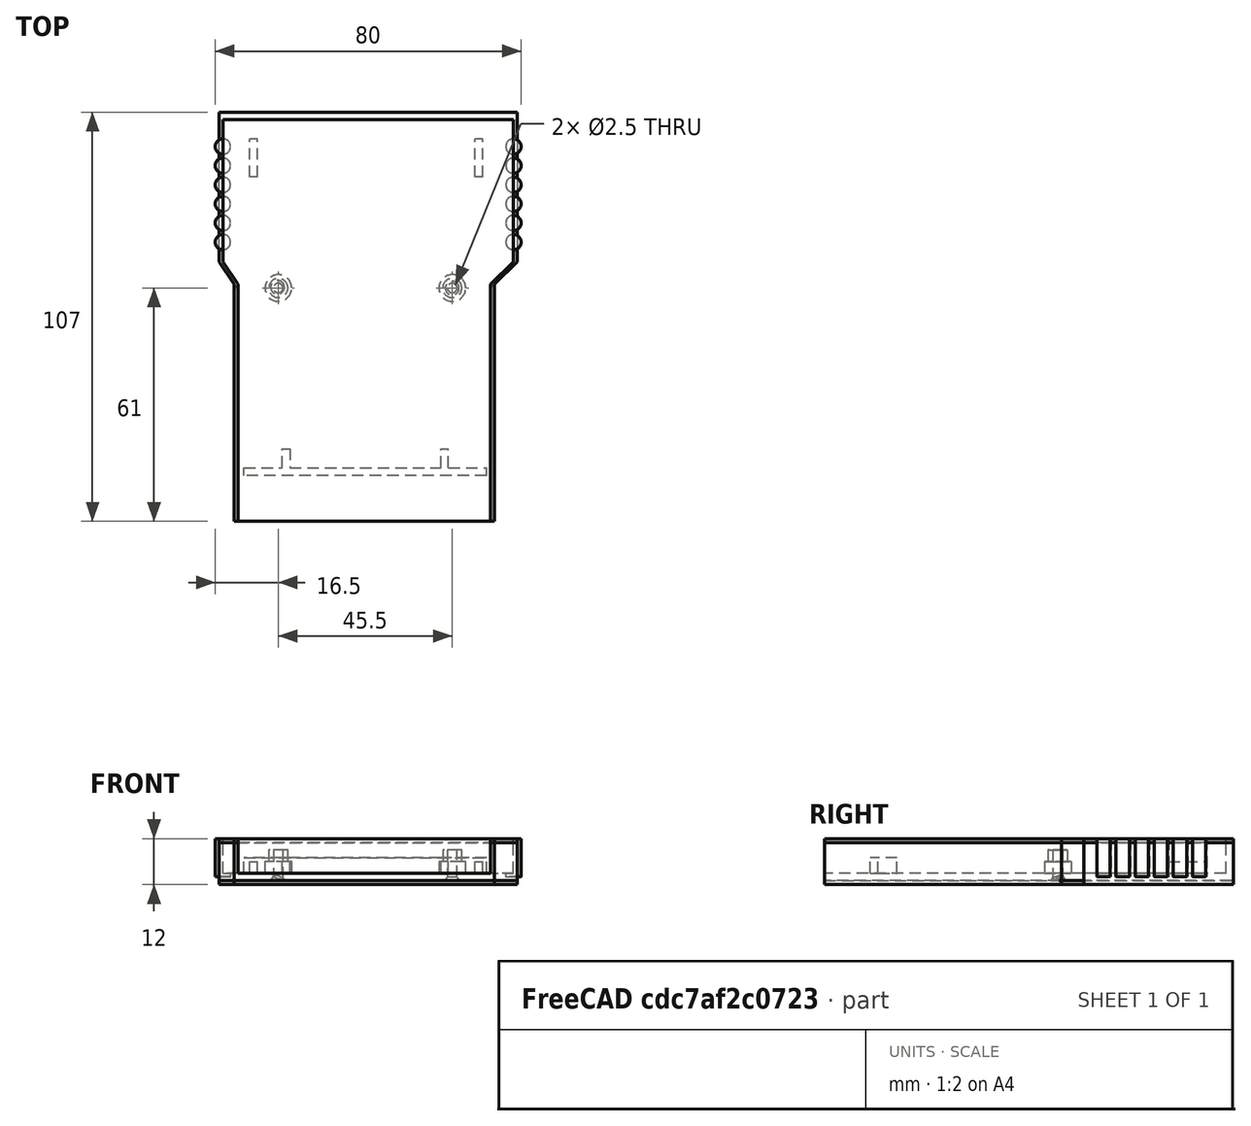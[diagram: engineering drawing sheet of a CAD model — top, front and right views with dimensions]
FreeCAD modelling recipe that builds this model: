
FCSTD DOCUMENT  (FreeCAD 0.20R29410 (Git))
Label: RTO11a_Cart_Bottom
License: All rights reserved
LicenseURL: http://en.wikipedia.org/wiki/All_rights_reserved
objects: Part::Cylinder×18, Part::MultiFuse×11, Part::Cut×8, Part::Fillet×5, Part::Box×4, PartDesign::Pad×4, Sketcher::SketchObject×3, Part::Cone×2, PartDesign::Body×2, Mesh::Feature×1, Part::Feature×1
note: 62 computed .brp shape members not serialized (recipe doc carries the construction recipe); baked Part::Feature solids carry a one-line shape summary decoded from their .brp

FEATURE [Part::Cylinder] Cylinder001  label="Cilindro"
  Angle = 360
  AttacherType = Attacher::AttachEngine3D
  FirstAngle = 0
  Height = 16
  Placement = pos=(-11,61,-2) rot=(0,0,1;0rad)
  Radius = 1.25
  SecondAngle = 0
FEATURE [Part::Cylinder] Cylinder002  label="Cilindro001"
  Angle = 360
  AttacherType = Attacher::AttachEngine3D
  FirstAngle = 0
  Height = 20
  Placement = pos=(-56.5,61,-2) rot=(0,0,1;0rad)
  Radius = 1.25
  SecondAngle = 0
FEATURE [Part::Cone] Cone  label="Cono"
  Angle = 360
  AttacherType = Attacher::AttachEngine3D
  Height = 5
  Placement = pos=(-11,61,-2) rot=(0,0,1;3.14159rad)
  Radius1 = 3
  Radius2 = 0
FEATURE [Part::Cone] Cone001  label="Cono001"
  Angle = 360
  AttacherType = Attacher::AttachEngine3D
  Height = 5
  Placement = pos=(-56.7,61.2,-2) rot=(0,0,1;0.017453rad)
  Radius1 = 3
  Radius2 = 0
FEATURE [Part::Box] Box001  label="Cubo001"
  AttacherType = Attacher::AttachEngine3D
  Height = 4
  Length = 2
  Placement = pos=(-64,90,1) rot=(0,0,1;0rad)
  Width = 10
FEATURE [Part::Cylinder] Cylinder003  label="Cilindro002"
  Angle = 360
  AttacherType = Attacher::AttachEngine3D
  FirstAngle = 0
  Height = 4
  Placement = pos=(-11,61,1) rot=(0,0,1;0rad)
  Radius = 3.5
  SecondAngle = 0
FEATURE [Part::MultiFuse] Fusion003
  Shapes = -> [Cylinder003,Box001]
FEATURE [Part::Cylinder] Cylinder004  label="Cilindro003"
  Angle = 360
  AttacherType = Attacher::AttachEngine3D
  FirstAngle = 0
  Height = 4
  Placement = pos=(-11,61,4) rot=(0,0,1;0rad)
  Radius = 2.5
  SecondAngle = 0
FEATURE [Part::MultiFuse] Fusion004
  Shapes = -> [Fusion003,Cylinder004]
FEATURE [Part::Cylinder] Cylinder  label="Cilindro004"
  Angle = 360
  AttacherType = Attacher::AttachEngine3D
  FirstAngle = 0
  Height = 4
  Placement = pos=(-56.5,61,1) rot=(0,0,1;0rad)
  Radius = 3.5
  SecondAngle = 0
FEATURE [Part::Cylinder] Cylinder005  label="Cilindro005"
  Angle = 360
  AttacherType = Attacher::AttachEngine3D
  FirstAngle = 0
  Height = 3
  Placement = pos=(-56.5,61,5) rot=(0,0,1;0rad)
  Radius = 2.5
  SecondAngle = 0
FEATURE [Sketcher::SketchObject] Sketch004
  AttachmentOffset = pos=(0,0,1) rot=(0,0,1;0rad)
  FullyConstrained = true
  MapMode = 5
  Placement = pos=(0,0,1) rot=(0,0,1;0rad)
  Support = -> [XY_Plane]
  sketch-geometry (12):
    g0: LineSegment StartX=-65.5 StartY=12 StartZ=0 EndX=-2 EndY=12 EndZ=0
    g1: LineSegment StartX=-2 StartY=14 StartZ=0 EndX=-12 EndY=14 EndZ=0
    g2: LineSegment StartX=-12 StartY=19 StartZ=0 EndX=-14 EndY=19 EndZ=0
    g3: LineSegment StartX=-12 StartY=19 StartZ=0 EndX=-12 EndY=14 EndZ=0
    g4: LineSegment StartX=-14 StartY=19 StartZ=0 EndX=-14 EndY=14 EndZ=0
    g5: LineSegment StartX=-14 StartY=14 StartZ=0 EndX=-53.5 EndY=14 EndZ=0
    g6: LineSegment StartX=-53.5 StartY=14 StartZ=0 EndX=-53.5 EndY=19 EndZ=0
    g7: LineSegment StartX=-53.5 StartY=19 StartZ=0 EndX=-55.5 EndY=19 EndZ=0
    g8: LineSegment StartX=-55.5 StartY=19 StartZ=0 EndX=-55.5 EndY=14 EndZ=0
    g9: LineSegment StartX=-55.5 StartY=14 StartZ=0 EndX=-65.5 EndY=14 EndZ=0
    g10: LineSegment StartX=-65.5 StartY=14 StartZ=0 EndX=-65.5 EndY=12 EndZ=0
    g11: LineSegment StartX=-2 StartY=14 StartZ=0 EndX=-2 EndY=12 EndZ=0
  constraints (36):
    c: Horizontal(g0)
    c: Horizontal(g1)
    c: Coincident(g3,g2)
    c: Coincident(g3,g1)
    c: Coincident(g4,g2)
    c: Vertical(g4)
    c: Coincident(g5,g4)
    c: Horizontal(g5)
    c: Coincident(g6,g5)
    c: Vertical(g6)
    c: Coincident(g7,g6)
    c: Coincident(g7,g8)
    c: Vertical(g8)
    c: Coincident(g8,g9)
    c: Horizontal(g9)
    c: Coincident(g9,g10)
    c: Coincident(g10,g0)
    c: Horizontal(g7)
    c: Vertical(g10)
    c: Vertical(g3)
    c: DistanceY(g0,g9) = 2
    c: DistanceX(g7,g7) = 2
    c: DistanceX(g2,g2) = 2
    c: DistanceY(g4,g4) = 5
    c: DistanceY(g0,g1) = 2
    c: DistanceY(g8,g5) = 0
    c: Horizontal(g2)
    c: DistanceX(g0,g0) = 63.5
    c: DistanceX(g9,g9) = 10
    c: DistanceX(g1,g1) = 10
    c: DistanceY(g8,g8) = 5
    c: Coincident(g11,g1)
    c: Coincident(g11,g0)
    c: Vertical(g11)
    c: DistanceY(g-1,g0) = 12
    c: DistanceX(g0,g-1) = 2
FEATURE [PartDesign::Pad] Pad013  label="front_bar"
  Direction = (0,0,1)
  Length = 5
  Length2 = 10
  Profile = -> Sketch004
  ReferenceAxis = -> Sketch004 [N_Axis]
  Type = 0
FEATURE [Sketcher::SketchObject] Sketch
  FullyConstrained = true
  MapMode = 5
  Support = -> [XY_Plane]
  sketch-geometry (8):
    g0: LineSegment StartX=0 StartY=0 StartZ=0 EndX=-68 EndY=0 EndZ=0
    g1: LineSegment StartX=-68 StartY=0 StartZ=0 EndX=-68 EndY=62 EndZ=0
    g2: LineSegment StartX=-68 StartY=62 StartZ=0 EndX=-72 EndY=67.82 EndZ=0
    g3: LineSegment StartX=-72 StartY=67.82 StartZ=0 EndX=-72 EndY=107 EndZ=0
    g4: LineSegment StartX=-72 StartY=107 StartZ=0 EndX=6 EndY=107 EndZ=0
    g5: LineSegment StartX=6 StartY=107 StartZ=0 EndX=6 EndY=67.82 EndZ=0
    g6: LineSegment StartX=6 StartY=67.82 StartZ=0 EndX=0 EndY=62 EndZ=0
    g7: LineSegment StartX=0 StartY=62 StartZ=0 EndX=0 EndY=0 EndZ=0
  constraints (24):
    c: PointOnObject(g0,g-2)
    c: PointOnObject(g0,g-1)
    c: Horizontal(g0)
    c: Coincident(g0,g1)
    c: Vertical(g1)
    c: Coincident(g1,g2)
    c: Coincident(g2,g3)
    c: Vertical(g3)
    c: Coincident(g3,g4)
    c: Horizontal(g4)
    c: Coincident(g4,g5)
    c: Vertical(g5)
    c: Coincident(g5,g6)
    c: PointOnObject(g6,g-2)
    c: Coincident(g6,g7)
    c: DistanceY(g1,g1) = 62
    c: DistanceY(g7,g7) = 62
    c: Coincident(g0,g7)
    c: DistanceX(g4,g4) = 78
    c: DistanceX(g0,g0) = 68
    c: Distance(g1,g4) = 45
    c: DistanceX(g2,g1) = 4
    c: DistanceY(g5,g2) = 0
    c: DistanceY(g6,g5) = 5.82
FEATURE [PartDesign::Pad] Pad
  BaseFeature = -> Pad013
  Direction = (0,0,1)
  Length = 11
  Length2 = 10
  Profile = -> Sketch
  ReferenceAxis = -> Sketch [N_Axis]
  Type = 0
FEATURE [Sketcher::SketchObject] Sketch005
  AttachmentOffset = pos=(-1,0,2) rot=(0,0,1;0rad)
  FullyConstrained = true
  MapMode = 5
  Placement = pos=(-1,0,2) rot=(0,0,1;0rad)
  Support = -> [XY_Plane002]
  sketch-geometry (8):
    g0: LineSegment StartX=0 StartY=0 StartZ=0 EndX=-66 EndY=0 EndZ=0
    g1: LineSegment StartX=-66 StartY=0 StartZ=0 EndX=-66 EndY=62 EndZ=0
    g2: LineSegment StartX=-66 StartY=62 StartZ=0 EndX=-70 EndY=67.82 EndZ=0
    g3: LineSegment StartX=-70 StartY=67.82 StartZ=0 EndX=-70 EndY=105 EndZ=0
    g4: LineSegment StartX=-70 StartY=105 StartZ=0 EndX=6 EndY=105 EndZ=0
    g5: LineSegment StartX=6 StartY=105 StartZ=0 EndX=6 EndY=67.82 EndZ=0
    g6: LineSegment StartX=6 StartY=67.82 StartZ=0 EndX=0 EndY=62 EndZ=0
    g7: LineSegment StartX=0 StartY=62 StartZ=0 EndX=0 EndY=0 EndZ=0
  constraints (24):
    c: PointOnObject(g0,g-2)
    c: PointOnObject(g0,g-1)
    c: Horizontal(g0)
    c: Coincident(g0,g1)
    c: Vertical(g1)
    c: Coincident(g1,g2)
    c: Coincident(g2,g3)
    c: Vertical(g3)
    c: Coincident(g3,g4)
    c: Horizontal(g4)
    c: Coincident(g4,g5)
    c: Vertical(g5)
    c: Coincident(g5,g6)
    c: PointOnObject(g6,g-2)
    c: Coincident(g6,g7)
    c: DistanceY(g1,g1) = 62
    c: DistanceY(g7,g7) = 62
    c: Coincident(g0,g7)
    c: DistanceX(g4,g4) = 76
    c: DistanceX(g0,g0) = 66
    c: Distance(g1,g4) = 43
    c: DistanceX(g2,g1) = 4
    c: DistanceY(g5,g2) = 0
    c: DistanceY(g6,g5) = 5.82
FEATURE [PartDesign::Pad] Pad014
  BaseFeature = -> Pad
  Direction = (0,0,1)
  Length = 10
  Length2 = 10
  Profile = -> Sketch005
  ReferenceAxis = -> Sketch005 [N_Axis]
  Type = 0
FEATURE [PartDesign::Body] Body001  label="slot"
  Origin = -> Origin
  Placement = pos=(0,0,-1) rot=(0,0,1;0rad)
  Tip = -> Pad014
FEATURE [PartDesign::Pad] Pad015
  Direction = (0,0,1)
  Length = 10
  Length2 = 10
  Profile = -> Sketch005
  ReferenceAxis = -> Sketch005 [N_Axis]
  Type = 0
FEATURE [PartDesign::Body] Body  label="Base"
  Group = -> [Sketch005,Pad015]
  Origin = -> Origin001
  Tip = -> Pad015
FEATURE [Part::Cut] Cut013  label="Basevuota"
  Base = -> Pad014
  Tool = -> Body
FEATURE [Part::Box] Box  label="Cubo"
  AttacherType = Attacher::AttachEngine3D
  Height = 4
  Length = 2
  Placement = pos=(-5,90,1) rot=(0,0,1;0rad)
  Width = 10
FEATURE [Part::Cylinder] Cylinder006  label="Cilindro006"
  Angle = 360
  AttacherType = Attacher::AttachEngine3D
  FirstAngle = 0
  Height = 10
  Placement = pos=(5,78,1) rot=(0,0,1;0rad)
  Radius = 2
  SecondAngle = 0
FEATURE [Part::Cylinder] Cylinder007  label="Cilindro007"
  Angle = 360
  AttacherType = Attacher::AttachEngine3D
  FirstAngle = 0
  Height = 10
  Placement = pos=(5,73,1) rot=(0,0,1;0rad)
  Radius = 2
  SecondAngle = 0
FEATURE [Part::Cylinder] Cylinder008  label="Cilindro008"
  Angle = 360
  AttacherType = Attacher::AttachEngine3D
  FirstAngle = 0
  Height = 10
  Placement = pos=(5,83,1) rot=(0,0,1;0rad)
  Radius = 2
  SecondAngle = 0
FEATURE [Part::Cylinder] Cylinder009  label="Cilindro009"
  Angle = 360
  AttacherType = Attacher::AttachEngine3D
  FirstAngle = 0
  Height = 10
  Placement = pos=(5,88,1) rot=(0,0,1;0rad)
  Radius = 2
  SecondAngle = 0
FEATURE [Part::Cylinder] Cylinder010  label="Cilindro010"
  Angle = 360
  AttacherType = Attacher::AttachEngine3D
  FirstAngle = 0
  Height = 10
  Placement = pos=(5,93,1) rot=(0,0,1;0rad)
  Radius = 2
  SecondAngle = 0
FEATURE [Part::Cylinder] Cylinder011  label="Cilindro011"
  Angle = 360
  AttacherType = Attacher::AttachEngine3D
  FirstAngle = 0
  Height = 10
  Placement = pos=(5,98,1) rot=(0,0,1;0rad)
  Radius = 2
  SecondAngle = 0
FEATURE [Part::MultiFuse] Fusion009  label="cil_rx"
  Shapes = -> [Cylinder006,Cylinder007,Cylinder008,Cylinder009,Cylinder010,Cylinder011]
FEATURE [Part::Cylinder] Cylinder012  label="Cilindro012"
  Angle = 360
  AttacherType = Attacher::AttachEngine3D
  FirstAngle = 0
  Height = 10
  Placement = pos=(5,78,1) rot=(0,0,1;0rad)
  Radius = 2
  SecondAngle = 0
FEATURE [Part::Cylinder] Cylinder013  label="Cilindro013"
  Angle = 360
  AttacherType = Attacher::AttachEngine3D
  FirstAngle = 0
  Height = 10
  Placement = pos=(5,73,1) rot=(0,0,1;0rad)
  Radius = 2
  SecondAngle = 0
FEATURE [Part::Cylinder] Cylinder014  label="Cilindro014"
  Angle = 360
  AttacherType = Attacher::AttachEngine3D
  FirstAngle = 0
  Height = 10
  Placement = pos=(5,83,1) rot=(0,0,1;0rad)
  Radius = 2
  SecondAngle = 0
FEATURE [Part::Cylinder] Cylinder015  label="Cilindro015"
  Angle = 360
  AttacherType = Attacher::AttachEngine3D
  FirstAngle = 0
  Height = 10
  Placement = pos=(5,88,1) rot=(0,0,1;0rad)
  Radius = 2
  SecondAngle = 0
FEATURE [Part::Cylinder] Cylinder016  label="Cilindro016"
  Angle = 360
  AttacherType = Attacher::AttachEngine3D
  FirstAngle = 0
  Height = 10
  Placement = pos=(5,93,1) rot=(0,0,1;0rad)
  Radius = 2
  SecondAngle = 0
FEATURE [Part::Cylinder] Cylinder017  label="Cilindro017"
  Angle = 360
  AttacherType = Attacher::AttachEngine3D
  FirstAngle = 0
  Height = 10
  Placement = pos=(5,98,1) rot=(0,0,1;0rad)
  Radius = 2
  SecondAngle = 0
FEATURE [Part::MultiFuse] Fusion010  label="cil_sx"
  Placement = pos=(-76,0,0) rot=(0,0,1;0rad)
  Shapes = -> [Cylinder012,Cylinder013,Cylinder014,Cylinder015,Cylinder016,Cylinder017]
FEATURE [Part::MultiFuse] Fusion011
  Shapes = -> [Fusion009,Fusion010]
FEATURE [Part::Box] Box002  label="Cubo002"
  AttacherType = Attacher::AttachEngine3D
  Height = 12
  Length = 5
  Placement = pos=(0,69,2) rot=(0,0,1;0rad)
  Width = 35
FEATURE [Part::Box] Box003  label="Cubo003"
  AttacherType = Attacher::AttachEngine3D
  Height = 12
  Length = 5
  Placement = pos=(-71,69,2) rot=(0,0,1;0rad)
  Width = 35
FEATURE [Part::Cut] Cut014
  Base = -> Fusion011
  Tool = -> Box002
FEATURE [Part::MultiFuse] Fusion
  Shapes = -> [Cut013,Cylinder]
FEATURE [Part::MultiFuse] Fusion012
  Shapes = -> [Fusion,Cylinder005]
FEATURE [Part::MultiFuse] Fusion013
  Shapes = -> [Fusion012,Fusion004]
FEATURE [Part::MultiFuse] Fusion014
  Shapes = -> [Fusion013,Box]
FEATURE [Part::MultiFuse] Fusion015
  Shapes = -> [Fusion014,Pad013]
FEATURE [Part::Cut] Cut
  Base = -> Cut014
  Tool = -> Box003
FEATURE [Part::MultiFuse] Fusion016
  Shapes = -> [Fusion015,Cut]
FEATURE [Part::Cut] Cut016
  Base = -> Fusion016
  Tool = -> Cylinder002
FEATURE [Part::Cut] Cut017
  Base = -> Cut016
  Tool = -> Cylinder001
FEATURE [Part::Cut] Cut018
  Base = -> Cut017
  Tool = -> Cone001
FEATURE [Part::Cut] Cut019  label="Bottom"
  Base = -> Cut018
  Tool = -> Cone
FEATURE [Part::Cut] Cut015  label="Final"
  Base = -> Cut014
  Tool = -> Box003
FEATURE [Part::Fillet] Fillet
  Base = -> Cut019
  Edges = 1 edges r=0.6: [Edge174]
FEATURE [Part::Fillet] Fillet001
  Base = -> Fillet
  Edges = 1 edges r=0.6: [Edge10]
FEATURE [Part::Fillet] Fillet002
  Base = -> Fillet001
  Edges = 1 edges r=0.6: [Edge16]
FEATURE [Part::Fillet] Fillet003
  Base = -> Fillet002
  Edges = 1 edges r=0.6: [Edge10]
FEATURE [Part::Fillet] Fillet004  label="Bot__final"
  Base = -> Fillet003
  Edges = 1 edges r=0.6: [Edge1]
FEATURE [Mesh::Feature] Mesh  label="Bot__final (Meshed)"
FEATURE [Part::Feature] Refined_Mesh_Solid_81622
  shape: bbox 80 x 107 x 11 mm, 687 faces, 0 solids (baked)
